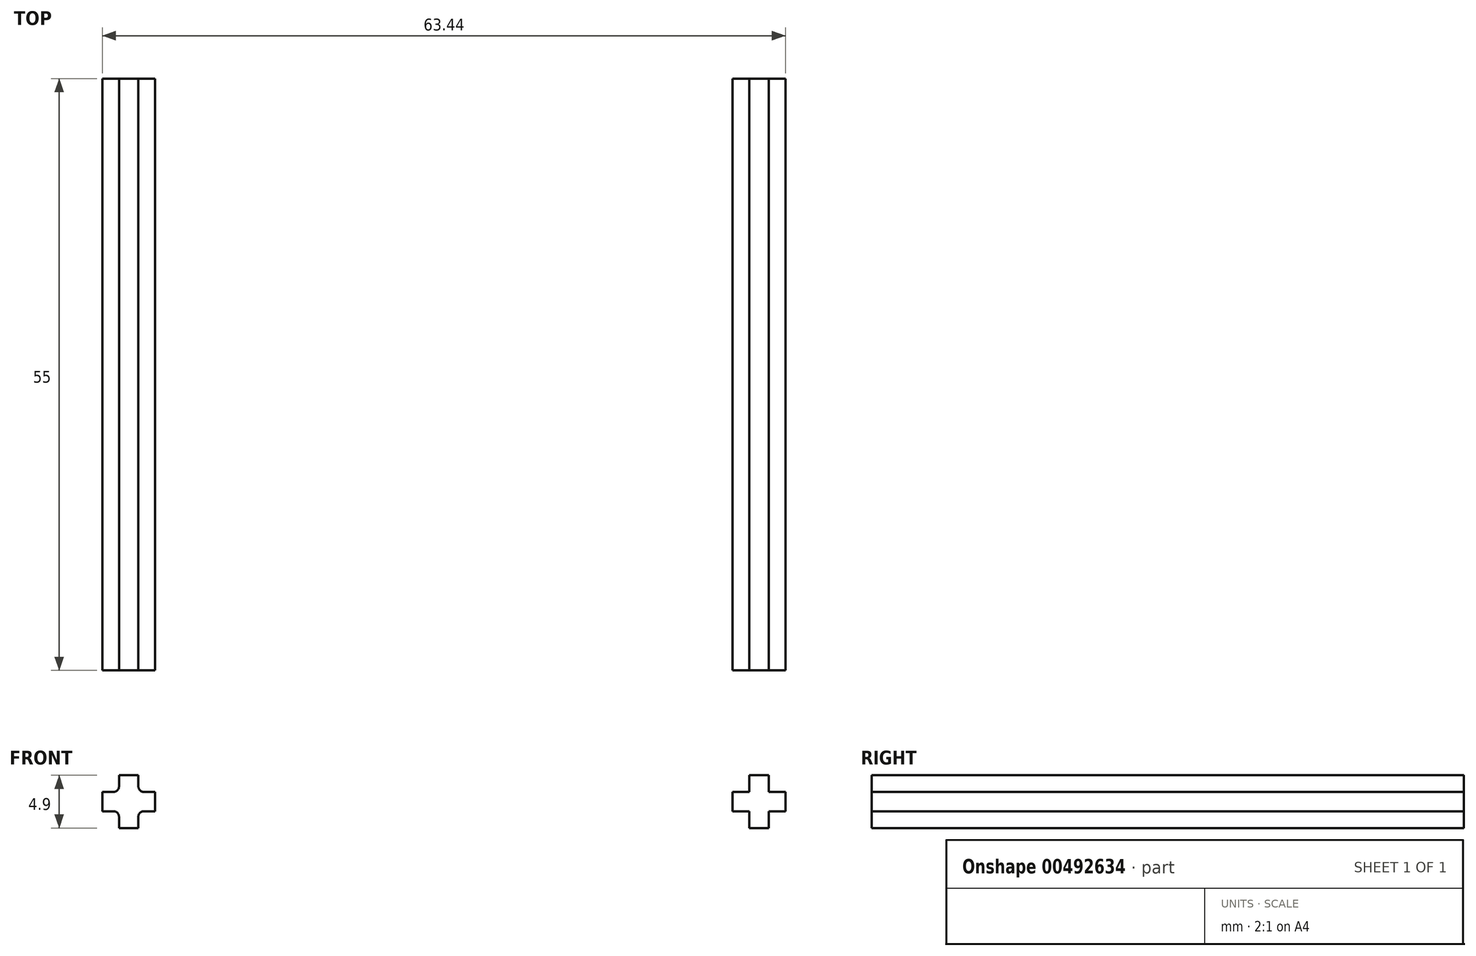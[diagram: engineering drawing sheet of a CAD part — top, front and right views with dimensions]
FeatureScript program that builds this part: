
annotation { "Feature Type Name" : "Feature", "Feature Type Description" : "" }
export const myFeature = defineFeature(function(context is Context, id is Id, definition is map)
    precondition{}
    {
        {
            var Q0;
            Q0=qCreatedBy(makeId("Front.planeOp"),FACE);
            var sketch = newSketch(context, id + "F0", { "sketchPlane" : qUnion([Q0])});
            skLineSegment(sketch, "E0.MirrorCS", {"start": v(-49.06, 27.44) * mm, "end": v(-53.96, 27.44) * mm});
            skLineSegment(sketch, "E1.MirrorCS", {"start": v(-49.06, 25.64) * mm, "end": v(-53.96, 25.64) * mm});
            skLineSegment(sketch, "E2", {"start": v(-53.96, 27.44) * mm, "end": v(-53.96, 25.64) * mm});
            skLineSegment(sketch, "E3", {"start": v(-49.06, 27.44) * mm, "end": v(-49.06, 25.64) * mm});
            skLineSegment(sketch, "E4.MirrorCS", {"start": v(-52.4, 29) * mm, "end": v(-52.4, 24.1) * mm});
            skLineSegment(sketch, "E5.MirrorCS", {"start": v(-50.6, 29) * mm, "end": v(-50.6, 24.1) * mm});
            skLineSegment(sketch, "E6", {"start": v(-52.4, 24.1) * mm, "end": v(-50.6, 24.1) * mm});
            skLineSegment(sketch, "E7", {"start": v(-52.4, 29) * mm, "end": v(-50.6, 29) * mm});
            skLineSegment(sketch, "E8.MirrorCS", {"start": v(9.48, 27.44) * mm, "end": v(9.48, 25.64) * mm});
            skLineSegment(sketch, "E9.MirrorCS", {"start": v(4.58, 27.44) * mm, "end": v(4.58, 25.64) * mm});
            skLineSegment(sketch, "E10.MirrorCS", {"start": v(7.93, 29) * mm, "end": v(6.13, 29) * mm});
            skLineSegment(sketch, "E11.MirrorCS", {"start": v(7.93, 24.1) * mm, "end": v(6.13, 24.1) * mm});
            skLineSegment(sketch, "E12.MirrorCS", {"start": v(6.13, 29) * mm, "end": v(6.13, 24.1) * mm});
            skLineSegment(sketch, "E13.MirrorCS", {"start": v(4.58, 25.64) * mm, "end": v(9.48, 25.64) * mm});
            skLineSegment(sketch, "E14.MirrorCS", {"start": v(7.93, 29) * mm, "end": v(7.93, 24.1) * mm});
            skLineSegment(sketch, "E15.MirrorCS", {"start": v(4.58, 27.44) * mm, "end": v(9.48, 27.44) * mm});
            skSolve(sketch);
        }
        {
            var Q0;
            Q0 = qSketchRegion(id + "F0", true);
            extrude(context, id + "F1", {"entities" : qUnion([Q0]), "depth" : 55 * mm, "offsetDistance" : 25 * mm});
        }
        {
            var Q0;
            Q0=makeQuery(id+"F1.opExtrude","SWEPT_EDGE",EDGE,{"disambiguationData":[OSD([sQuery(id+"F0.wireOp",EDGE,"E0.MirrorCS"),sQuery(id+"F0.wireOp",EDGE,"E5.MirrorCS")])]});
            var Q1;
            Q1=makeQuery(id+"F1.opExtrude","SWEPT_EDGE",EDGE,{"disambiguationData":[OSD([sQuery(id+"F0.wireOp",EDGE,"E1.MirrorCS"),sQuery(id+"F0.wireOp",EDGE,"E5.MirrorCS")])]});
            var Q2;
            Q2=makeQuery(id+"F1.opExtrude","SWEPT_EDGE",EDGE,{"disambiguationData":[OSD([sQuery(id+"F0.wireOp",EDGE,"E0.MirrorCS"),sQuery(id+"F0.wireOp",EDGE,"E4.MirrorCS")])]});
            var Q3;
            Q3=makeQuery(id+"F1.opExtrude","SWEPT_EDGE",EDGE,{"disambiguationData":[OSD([sQuery(id+"F0.wireOp",EDGE,"E1.MirrorCS"),sQuery(id+"F0.wireOp",EDGE,"E4.MirrorCS")])]});
            fillet(context, id + "F2", {"entities" : qUnion([Q0, Q1, Q2, Q3]), "radius" : 0.5 * mm, "tangentPropagation" : true, "allowEdgeOverflow" : false});
        }
    });
